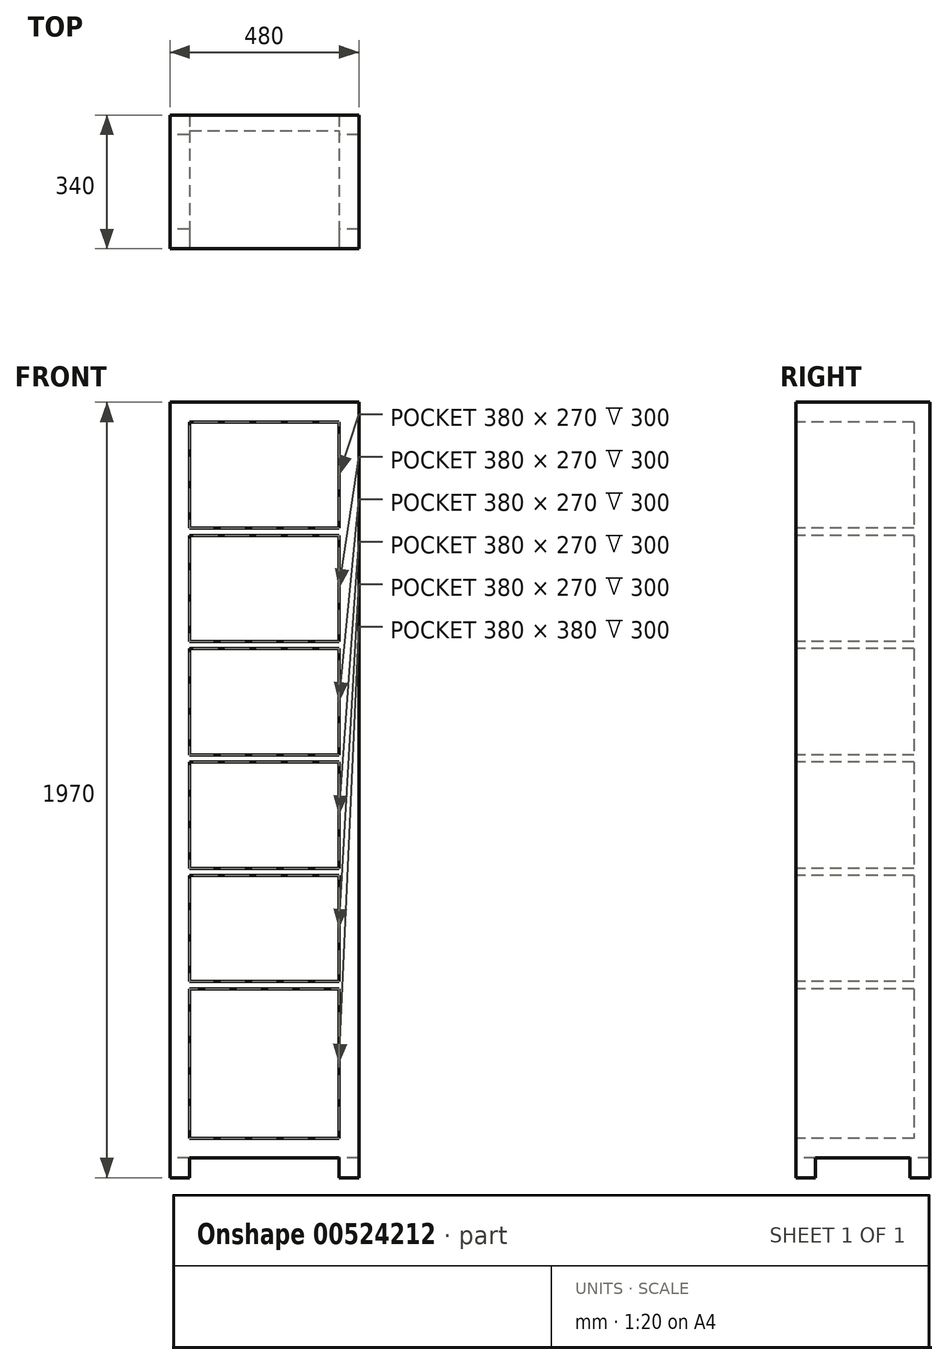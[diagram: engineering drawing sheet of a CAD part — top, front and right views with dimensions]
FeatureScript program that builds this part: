
annotation { "Feature Type Name" : "Feature", "Feature Type Description" : "" }
export const myFeature = defineFeature(function(context is Context, id is Id, definition is map)
    precondition{}
    {
        {
            var Q0;
            Q0=qCreatedBy(makeId("Top.planeOp"),FACE);
            var sketch = newSketch(context, id + "F0", { "sketchPlane" : qUnion([Q0])});
            skLineSegment(sketch, "E0.bottom", {"start": v(0, 0) * mm, "end": v(-480, 0) * mm});
            skLineSegment(sketch, "E0.top", {"start": v(0, 340) * mm, "end": v(-480, 340) * mm});
            skLineSegment(sketch, "E0.left", {"start": v(0, 0) * mm, "end": v(0, 340) * mm});
            skLineSegment(sketch, "E0.right", {"start": v(-480, 0) * mm, "end": v(-480, 340) * mm});
            skSolve(sketch);
        }
        {
            var Q0;
            Q0=qSketchRegion(id+"F0",true);
            extrude(context, id + "F1", {"entities" : qUnion([Q0]), "depth" : 1970 * mm, "offsetDistance" : 25 * mm});
        }
        {
            var Q0;
            Q0=makeQuery(id+"F1.opExtrude","SWEPT_FACE",FACE,{"disambiguationData":[OSD([sQuery(id+"F0.wireOp",EDGE,"E0.bottom")])]});
            var sketch = newSketch(context, id + "F2", { "sketchPlane" : qUnion([Q0])});
            skLineSegment(sketch, "E1.0", {"start": v(-480, 1970) * mm, "end": v(-480, 0) * mm});
            skLineSegment(sketch, "E2.0", {"start": v(0, 0) * mm, "end": v(-480, 0) * mm});
            skLineSegment(sketch, "E3.0", {"start": v(0, 1970) * mm, "end": v(0, 0) * mm});
            skLineSegment(sketch, "E4.0", {"start": v(0, 1970) * mm, "end": v(-480, 1970) * mm});
            skLineSegment(sketch, "E5.bottom", {"start": v(-430, 1920) * mm, "end": v(-50, 1920) * mm});
            skLineSegment(sketch, "E5.top", {"start": v(-430, 100) * mm, "end": v(-50, 100) * mm});
            skLineSegment(sketch, "E5.left", {"start": v(-430, 1920) * mm, "end": v(-430, 100) * mm});
            skLineSegment(sketch, "E5.right", {"start": v(-50, 1920) * mm, "end": v(-50, 100) * mm});
            skLineSegment(sketch, "E6.bottom", {"start": v(-430, 50) * mm, "end": v(-50, 50) * mm});
            skLineSegment(sketch, "E6.top", {"start": v(-430, 0) * mm, "end": v(-50, 0) * mm});
            skLineSegment(sketch, "E6.left", {"start": v(-430, 50) * mm, "end": v(-430, 0) * mm});
            skLineSegment(sketch, "E6.right", {"start": v(-50, 50) * mm, "end": v(-50, 0) * mm});
            skLineSegment(sketch, "E7.bottom", {"start": v(-430, 1650) * mm, "end": v(-50, 1650) * mm});
            skLineSegment(sketch, "E7.top", {"start": v(-430, 1632) * mm, "end": v(-50, 1632) * mm});
            skLineSegment(sketch, "E7.left", {"start": v(-430, 1650) * mm, "end": v(-430, 1632) * mm});
            skLineSegment(sketch, "E7.right", {"start": v(-50, 1650) * mm, "end": v(-50, 1632) * mm});
            skLineSegment(sketch, "E8.bottom", {"start": v(-430, 1362) * mm, "end": v(-50, 1362) * mm});
            skLineSegment(sketch, "E8.top", {"start": v(-430, 1344) * mm, "end": v(-50, 1344) * mm});
            skLineSegment(sketch, "E8.left", {"start": v(-430, 1362) * mm, "end": v(-430, 1344) * mm});
            skLineSegment(sketch, "E8.right", {"start": v(-50, 1362) * mm, "end": v(-50, 1344) * mm});
            skLineSegment(sketch, "E9.bottom", {"start": v(-430, 1074) * mm, "end": v(-50, 1074) * mm});
            skLineSegment(sketch, "E9.top", {"start": v(-430, 1056) * mm, "end": v(-50, 1056) * mm});
            skLineSegment(sketch, "E9.left", {"start": v(-430, 1074) * mm, "end": v(-430, 1056) * mm});
            skLineSegment(sketch, "E9.right", {"start": v(-50, 1074) * mm, "end": v(-50, 1056) * mm});
            skLineSegment(sketch, "E10.bottom", {"start": v(-430, 786) * mm, "end": v(-50, 786) * mm});
            skLineSegment(sketch, "E10.top", {"start": v(-430, 768) * mm, "end": v(-50, 768) * mm});
            skLineSegment(sketch, "E10.left", {"start": v(-430, 786) * mm, "end": v(-430, 768) * mm});
            skLineSegment(sketch, "E10.right", {"start": v(-50, 786) * mm, "end": v(-50, 768) * mm});
            skLineSegment(sketch, "E11.bottom", {"start": v(-430, 498) * mm, "end": v(-50, 498) * mm});
            skLineSegment(sketch, "E11.top", {"start": v(-430, 480) * mm, "end": v(-50, 480) * mm});
            skLineSegment(sketch, "E11.left", {"start": v(-430, 498) * mm, "end": v(-430, 480) * mm});
            skLineSegment(sketch, "E11.right", {"start": v(-50, 498) * mm, "end": v(-50, 480) * mm});
            skSolve(sketch);
        }
        {
            var Q0;
            Q0=makeQuery(id+"F2.imprint","IMPRINT",FACE,{"disambiguationData":[TD([[makeQuery(id+"F2.imprint","IMPRINT",EDGE,{"derivedFrom":sQuery(id+"F2.wireOp",EDGE,"E6.bottom")}),-1.0]])]});
            extrude(context, id + "F3", {"entities" : qUnion([Q0]), "operationType" : NewBodyOperationType.REMOVE, "oppositeDirection" : true, "depth" : 350 * mm, "offsetDistance" : 25 * mm});
        }
        {
            var Q0;
            {var subQ0=sQuery(id+"F2.wireOp",EDGE,"E5.top");Q0=makeQuery(id+"F2.imprint","IMPRINT",FACE,{"disambiguationData":[TD([[makeQuery(id+"F2.imprint","IMPRINT",EDGE,{"derivedFrom":subQ0}),1.0]])]});}
            var Q1;
            {var subQ0=sQuery(id+"F2.wireOp",EDGE,"E10.top");Q1=makeQuery(id+"F2.imprint","IMPRINT",FACE,{"disambiguationData":[TD([[makeQuery(id+"F2.imprint","IMPRINT",EDGE,{"derivedFrom":subQ0}),-1.0]])]});}
            var Q2;
            {var subQ0=sQuery(id+"F2.wireOp",EDGE,"E9.top");Q2=makeQuery(id+"F2.imprint","IMPRINT",FACE,{"disambiguationData":[TD([[makeQuery(id+"F2.imprint","IMPRINT",EDGE,{"derivedFrom":subQ0}),-1.0]])]});}
            var Q3;
            {var subQ0=sQuery(id+"F2.wireOp",EDGE,"E8.top");Q3=makeQuery(id+"F2.imprint","IMPRINT",FACE,{"disambiguationData":[TD([[makeQuery(id+"F2.imprint","IMPRINT",EDGE,{"derivedFrom":subQ0}),-1.0]])]});}
            var Q4;
            {var subQ0=sQuery(id+"F2.wireOp",EDGE,"E7.top");Q4=makeQuery(id+"F2.imprint","IMPRINT",FACE,{"disambiguationData":[TD([[makeQuery(id+"F2.imprint","IMPRINT",EDGE,{"derivedFrom":subQ0}),-1.0]])]});}
            var Q5;
            {var subQ0=sQuery(id+"F2.wireOp",EDGE,"E5.bottom");Q5=makeQuery(id+"F2.imprint","IMPRINT",FACE,{"disambiguationData":[TD([[makeQuery(id+"F2.imprint","IMPRINT",EDGE,{"derivedFrom":subQ0}),-1.0]])]});}
            extrude(context, id + "F4", {"entities" : qUnion([Q0, Q1, Q2, Q3, Q4, Q5]), "operationType" : NewBodyOperationType.REMOVE, "oppositeDirection" : true, "depth" : 300 * mm, "offsetDistance" : 25 * mm});
        }
        {
            var Q0;
            Q0=makeQuery(id+"F1.opExtrude","SWEPT_FACE",FACE,{"disambiguationData":[OSD([sQuery(id+"F0.wireOp",EDGE,"E0.right")])]});
            var sketch = newSketch(context, id + "F5", { "sketchPlane" : qUnion([Q0])});
            skLineSegment(sketch, "E12.0", {"start": v(-340, 1970) * mm, "end": v(-340, 0) * mm});
            skLineSegment(sketch, "E13.0", {"start": v(0, 0) * mm, "end": v(-340, 0) * mm});
            skLineSegment(sketch, "E14.0", {"start": v(0, 1920) * mm, "end": v(0, 100) * mm});
            skLineSegment(sketch, "E15.bottom", {"start": v(-290, 0) * mm, "end": v(-50, 0) * mm});
            skLineSegment(sketch, "E15.top", {"start": v(-290, 50) * mm, "end": v(-50, 50) * mm});
            skLineSegment(sketch, "E15.left", {"start": v(-290, 0) * mm, "end": v(-290, 50) * mm});
            skLineSegment(sketch, "E15.right", {"start": v(-50, 0) * mm, "end": v(-50, 50) * mm});
            skSolve(sketch);
        }
        {
            var Q0;
            Q0=makeQuery(id+"F5.imprint","IMPRINT",FACE,{"disambiguationData":[TD([[makeQuery(id+"F5.imprint","IMPRINT",EDGE,{"derivedFrom":sQuery(id+"F5.wireOp",EDGE,"E15.top")}),-1.0]])]});
            extrude(context, id + "F6", {"entities" : qUnion([Q0]), "operationType" : NewBodyOperationType.REMOVE, "oppositeDirection" : true, "depth" : 895 * mm, "offsetDistance" : 25 * mm});
        }
    });
